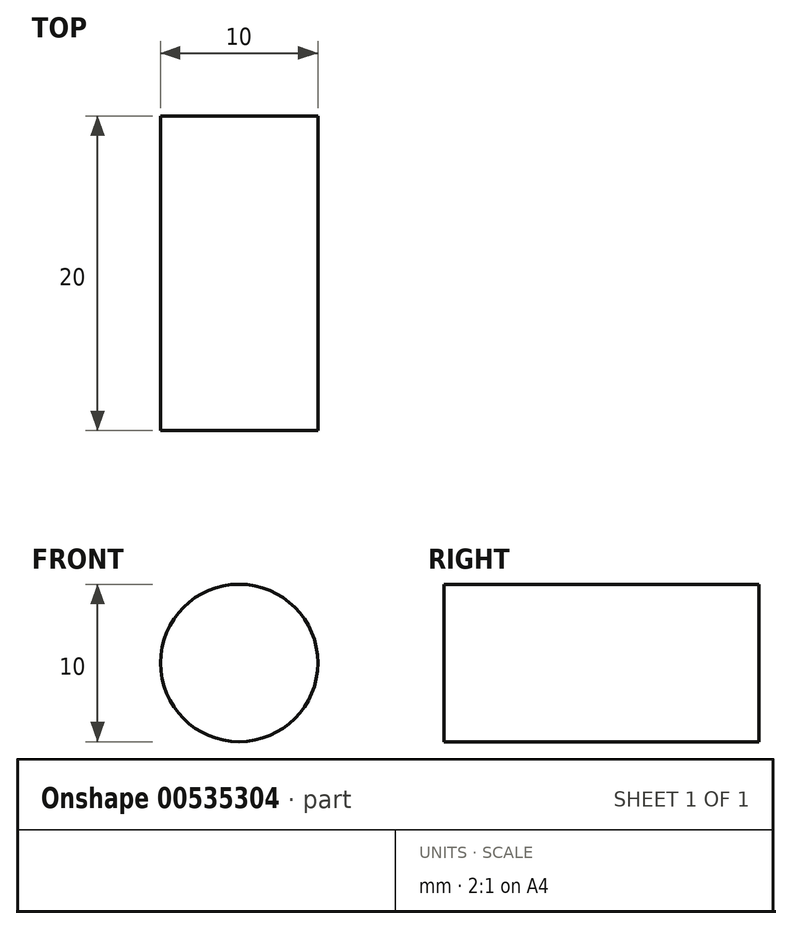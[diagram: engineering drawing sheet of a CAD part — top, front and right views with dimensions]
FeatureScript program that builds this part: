
annotation { "Feature Type Name" : "Feature", "Feature Type Description" : "" }
export const myFeature = defineFeature(function(context is Context, id is Id, definition is map)
    precondition{}
    {
        {
            var Q0;
            Q0=qCreatedBy(makeId("Front.planeOp"),FACE);
            var sketch = newSketch(context, id + "F0", { "sketchPlane" : qUnion([Q0])});
            skCircle(sketch, "E0", {"center": v(0, 0) * mm, "radius": 5 * mm});
            skSolve(sketch);
        }
        {
            var Q0;
            Q0=makeQuery(id+"F0.imprint","IMPRINT",FACE,{"disambiguationData":[TD([[makeQuery(id+"F0.imprint","IMPRINT",EDGE,{"derivedFrom":sQuery(id+"F0.wireOp",EDGE,"E0")}),1.0]])]});
            extrude(context, id + "F1", {"entities" : qUnion([Q0]), "depth" : 20 * mm, "offsetDistance" : 25 * mm});
        }
    });
